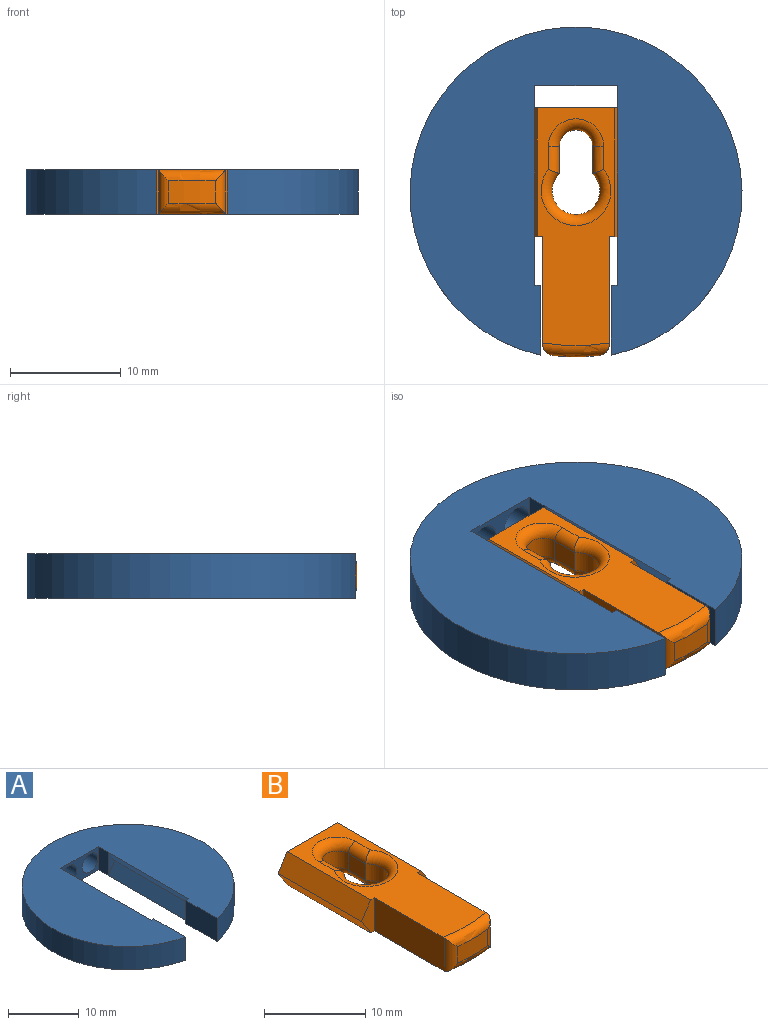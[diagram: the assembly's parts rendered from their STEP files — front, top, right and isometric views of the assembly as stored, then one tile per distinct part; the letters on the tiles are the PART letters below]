
ASSEMBLY  parts=2 mates=1
PART A: 20 faces, bbox 30x29.7x4 mm
  f0: plane 4x1.3mm, normal (0,-1,0), area 2.6mm2, adj f8,f12,f13
  f1: plane 30x29.65mm, normal (0,0,1), area 530.1mm2, adj f3,f5,f6,f9,f10,f11,f12,f13
  f2: plane 4x1.3mm, normal (0,-1,0), area 2.6mm2, adj f7,f11,f14
  f3: cylinder r=15mm len=30mm, axis (0,0,-1), area 351.2mm2, adj f1,f4,f9,f10
  f4: plane 30x29.65mm, normal (0,0,-1), area 530.1mm2, adj f3,f5,f6,f7,f8,f9,f10,f13
  f5: plane 4x1.84mm, normal (0,1,0), area 4.8mm2, adj f1,f4,f7,f9,f11
  f6: plane 4x1.84mm, normal (0,1,0), area 4.8mm2, adj f1,f4,f8,f10,f12
  f7: plane 16.05x2mm, normal (0.84,0,0.54), area 38.3mm2, adj f2,f4,f5,f11
  f8: plane 16.05x2mm, normal (-0.84,0,0.54), area 38.3mm2, adj f0,f4,f6,f12
  f9: plane 6.3x4mm, normal (1,0,0), area 25.2mm2, adj f1,f3,f4,f5
  f10: plane 6.3x4mm, normal (-1,0,0), area 25.2mm2, adj f1,f3,f4,f6
  f11: plane 16.05x2mm, normal (0.84,0,-0.54), area 38.3mm2, adj f1,f2,f5,f7
  f12: plane 16.05x2mm, normal (-0.84,0,-0.54), area 38.3mm2, adj f0,f1,f6,f8
  f13: plane 4x2mm, normal (-1,0,0), area 8mm2, adj f0,f1,f4,f15
  f14: plane 4x2mm, normal (1,0,0), area 8mm2, adj f1,f2,f4,f15
  f15: plane 7.48x4mm, normal (0,-1,0), area 14.3mm2, adj f1,f4,f13,f14,f17,f19
  f16: plane 3.15x3.15mm, normal (0,-1,0), area 7.8mm2, adj f17
  f17: cylinder r=1.57mm len=3.15mm, axis (0,-1,0), area 29.7mm2, adj f15,f16
  f18: plane 3.15x3.15mm, normal (0,-1,0), area 7.8mm2, adj f19
  f19: cylinder r=1.57mm len=3.15mm, axis (0,-1,0), area 29.7mm2, adj f15,f18
PART B: 32 faces, bbox 9.6x22.8x4 mm
  f0: plane 9.6x4mm, normal (0,1,0), area 17.6mm2, adj f7,f8,f9,f10,f11,f12,f16,f18
  f1: plane 4x1.8mm, normal (0,-1,0), area 4.6mm2, adj f7,f8,f9,f10,f15
  f2: plane 4x1.8mm, normal (0,-1,0), area 4.6mm2, adj f7,f8,f11,f12,f14
  f3: cylinder r=2.15mm len=4.3mm, axis (0,0,-1), area 20.4mm2, adj f4,f6,f22,f26
  f4: plane 2.46x2mm, normal (1,0,0), area 4.9mm2, adj f3,f5,f23,f24
  f5: cylinder r=1.5mm len=3mm, axis (0,0,-1), area 9.4mm2, adj f4,f6,f21,f25
  f6: plane 2.46x2mm, normal (-1,0,0), area 4.9mm2, adj f3,f5,f20,f27
  f7: plane 21.5x7mm, normal (0,0,1), area 93mm2, adj f0,f1,f2,f10,f12,f14,f15,f24
  f8: plane 21.5x7mm, normal (0,0,-1), area 93mm2, adj f0,f1,f2,f9,f11,f14,f15,f20
  f9: plane 11.65x2mm, normal (-0.84,0,-0.54), area 27.8mm2, adj f0,f1,f8,f10
  f10: plane 11.65x2mm, normal (-0.84,0,0.54), area 27.8mm2, adj f0,f1,f7,f9
  f11: plane 11.65x2mm, normal (0.84,0,-0.54), area 27.8mm2, adj f0,f2,f8,f12
  f12: plane 11.65x2mm, normal (0.84,0,0.54), area 27.8mm2, adj f0,f2,f7,f11
  f13: cylinder r=19mm len=4.22mm, axis (0,0,-1), area 8.5mm2, adj f28,f29,f30,f31
  f14: plane 9.74x4mm, normal (1,0,0), area 39mm2, adj f2,f7,f8,f28,f30,f31
  f15: plane 9.74x4mm, normal (-1,0,0), area 39mm2, adj f1,f7,f8,f28,f29,f31
  f16: cylinder r=1.57mm len=3.15mm, axis (0,-1,0), area 7.9mm2, adj f0,f17
  f17: plane 3.15x3.15mm, normal (0,1,0), area 7.8mm2, adj f16
  f18: cylinder r=1.57mm len=3.15mm, axis (0,-1,0), area 7.9mm2, adj f0,f19
  f19: plane 3.15x3.15mm, normal (0,1,0), area 7.8mm2, adj f18
  f20: cylinder r=1mm len=2.46mm, axis (0,-1,0), area 3.6mm2, adj f6,f8,f21,f22
  f21: torus R=2.5mm, axis (0,0,1), area 9.2mm2, adj f5,f8,f20,f23
  f22: torus R=3.15mm, axis (0,0,1), area 18.2mm2, adj f3,f8,f20,f23
  f23: cylinder r=1mm len=2.46mm, axis (0,1,0), area 3.6mm2, adj f4,f8,f21,f22
  f24: cylinder r=1mm len=2.46mm, axis (0,-1,0), area 3.6mm2, adj f4,f7,f25,f26
  f25: torus R=2.5mm, axis (0,0,1), area 9.2mm2, adj f5,f7,f24,f27
  f26: torus R=3.15mm, axis (0,0,1), area 18.2mm2, adj f3,f7,f24,f27
  f27: cylinder r=1mm len=2.46mm, axis (0,1,0), area 3.6mm2, adj f6,f7,f25,f26
  f28: torus R=18mm, axis (0,0,1), area 8.5mm2, adj f7,f13,f14,f15,f29,f30
  f29: cylinder r=1mm len=3.98mm, axis (0,0,-1), area 4.7mm2, adj f13,f15,f28,f31
  f30: cylinder r=1mm len=3.98mm, axis (0,0,-1), area 4.7mm2, adj f13,f14,f28,f31
  f31: torus R=18mm, axis (0,0,1), area 8.5mm2, adj f8,f13,f14,f15,f29,f30
PLACE A t=(0,-5.2,0)mm fixed
PLACE B t=(0,-1,0)mm
MATE slider B.f0 <-> A.f15  axis (0,1,0) through (0,2.5,0)mm
